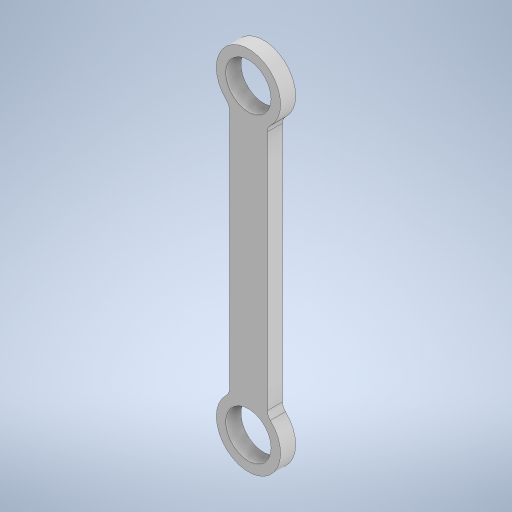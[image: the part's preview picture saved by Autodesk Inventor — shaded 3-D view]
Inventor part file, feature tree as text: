
AUTODESK INVENTOR PART (.ipt)
format: ipt  version: 2024.3 (Build 283343000, 343)  size: 321,536 bytes
history: native  units: mm
features: other x1, extrude x1, fillet x1, sketch x1
ambient origin geometry x8: Origin, YZ Plane, XZ Plane, XY Plane, X Axis, Y Axis, Z Axis, Center Point
bodies: Body1 (feature_tree)
feature tree (4):
  other  "ソリッド1"
  extrude  "押し出し1"  Depth=34.0mm
  fillet  "フィレット2"  Radius=24.0mm
  sketch  "スケッチ1"
